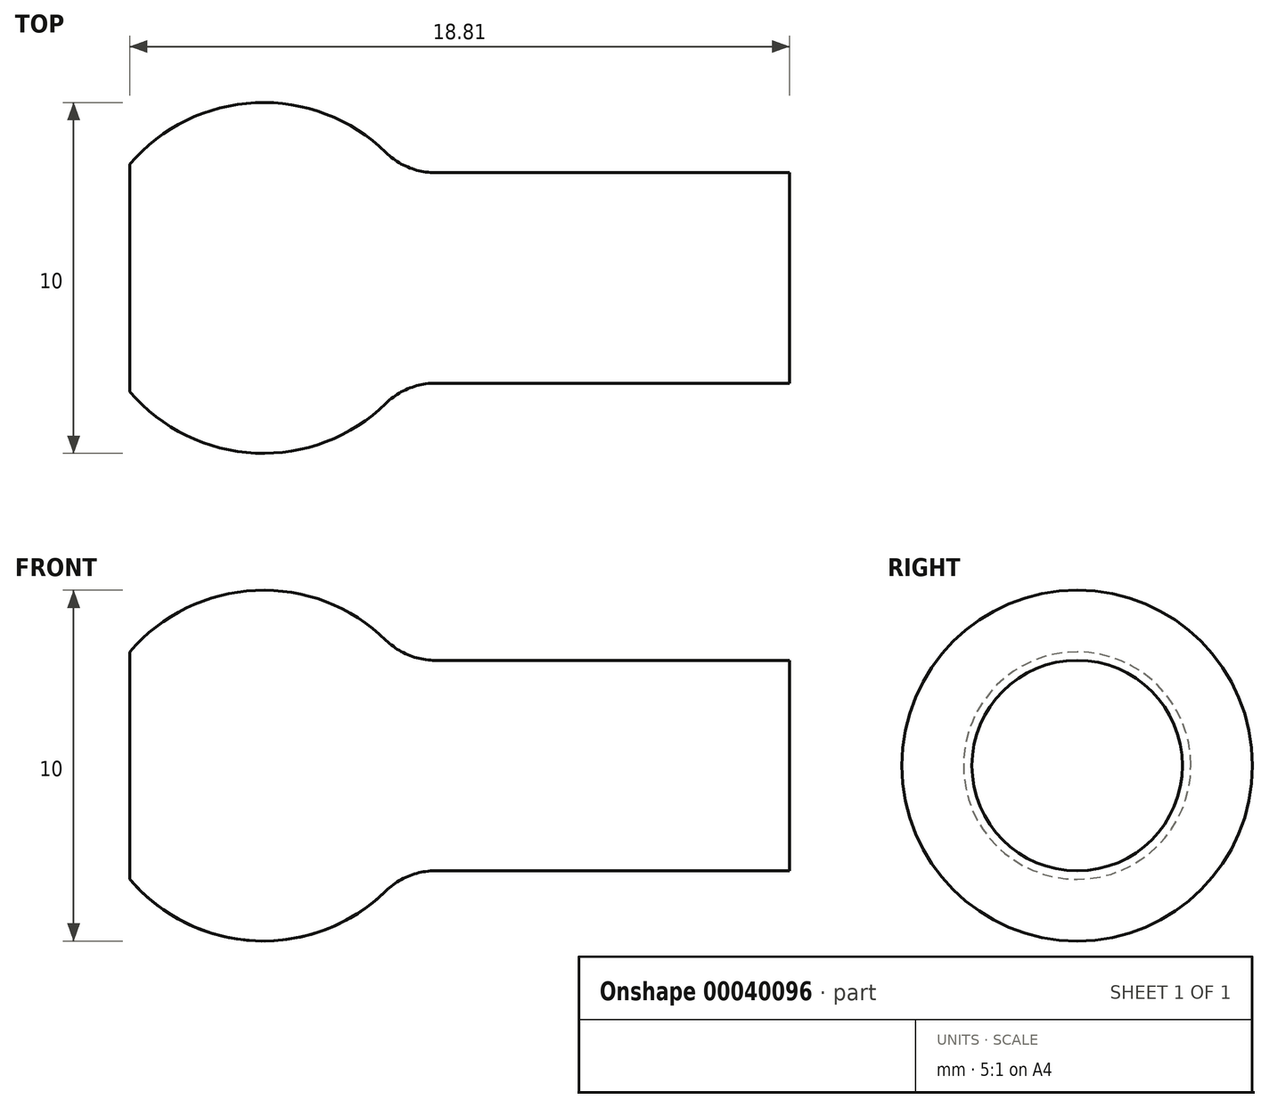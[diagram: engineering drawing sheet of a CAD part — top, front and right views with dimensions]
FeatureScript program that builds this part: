
annotation { "Feature Type Name" : "Feature", "Feature Type Description" : "" }
export const myFeature = defineFeature(function(context is Context, id is Id, definition is map)
    precondition{}
    {
        {
            var Q0;
            Q0=qCreatedBy(makeId("Front.planeOp"),FACE);
            var sketch = newSketch(context, id + "F0", { "sketchPlane" : qUnion([Q0])});
            skLineSegment(sketch, "E0", {"start": v(0, 0) * mm, "end": v(-18.8, 0) * mm});
            skLineSegment(sketch, "E1", {"start": v(0, 0) * mm, "end": v(0, -3) * mm});
            skLineSegment(sketch, "E2.0", {"start": v(0, -3) * mm, "end": v(-11, -3) * mm});
            skArc(sketch, "E3", {"start": v(-18.8, -3.24) * mm, "mid": v(-14.85, -5) * mm, "end": v(-11, -3) * mm});
            skLineSegment(sketch, "E4", {"start": v(-18.8, 0) * mm, "end": v(-18.8, -3.24) * mm});
            skSolve(sketch);
        }
        {
            var Q0;
            Q0 = qSketchRegion(id + "F0", true);
            var Q1;
            Q1=sQuery(id+"F0.wireOp",EDGE,"E0");
            revolve(context, id + "F1", {"entities" : qUnion([Q0]), "axis" : qUnion([Q1]), "revolveType" : RevolveType.FULL});
        }
        {
            var Q0;
            Q0=makeQuery(id+"F1.opRevolve","SWEPT_EDGE",EDGE,{"disambiguationData":[OSD([sQuery(id+"F0.wireOp",EDGE,"E2.0"),sQuery(id+"F0.wireOp",EDGE,"E3")])]});
            fillet(context, id + "F2", {"entities" : qUnion([Q0]), "radius" : 2 * mm, "tangentPropagation" : true, "allowEdgeOverflow" : false});
        }
    });
